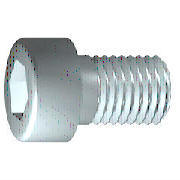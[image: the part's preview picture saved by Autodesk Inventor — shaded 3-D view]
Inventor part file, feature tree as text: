
AUTODESK INVENTOR PART (.ipt)
format: ipt  version: 2018 (Build 220112000, 112)  size: 184,320 bytes
history: native  units: mm (DEFAULTED — no unit token found)
features: sketch x2, other x1, extrude x1, plane x1, fillet x1
ambient origin geometry x7: Origin, YZ Plane, XY Plane, X Axis, Y Axis, Z Axis, Center Point
bodies: Solid1 (feature_tree)
feature tree (6):
  other  "Corpo"
  extrude  "Intaglio"  Depth=24.0mm
  plane  "Work Plane1"
  fillet  "Fillet2"  Radius=0.61355mm
  sketch  "Schizzo1"
  sketch  "Schizzo2"
